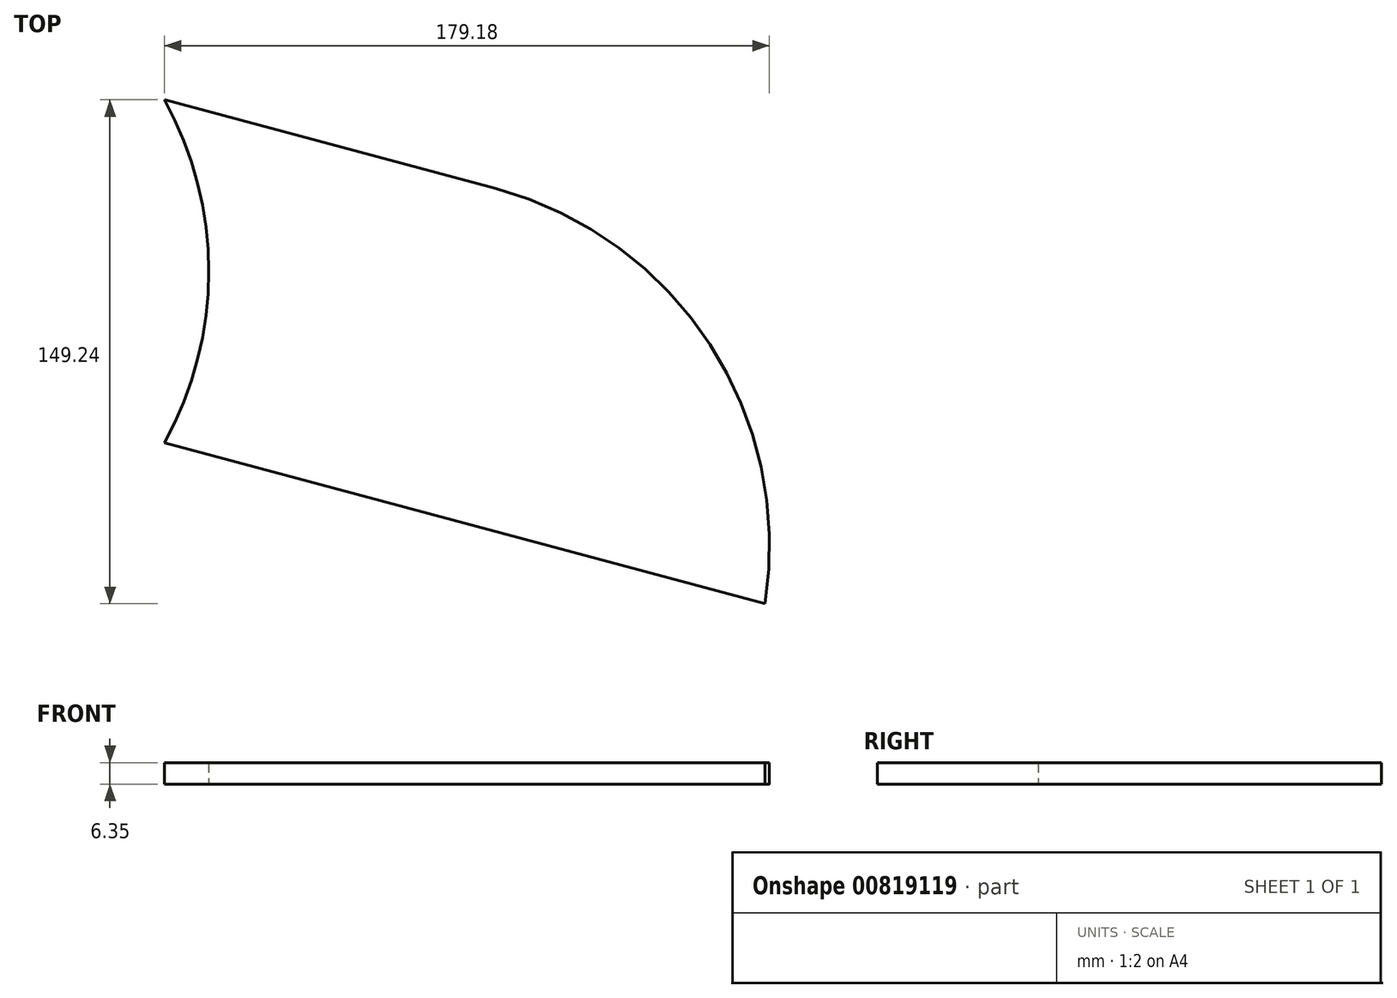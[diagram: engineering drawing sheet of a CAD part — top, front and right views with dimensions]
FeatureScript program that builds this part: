
annotation { "Feature Type Name" : "Feature", "Feature Type Description" : "" }
export const myFeature = defineFeature(function(context is Context, id is Id, definition is map)
    precondition{}
    {
        {
            var Q0;
            Q0=qCreatedBy(makeId("Top.planeOp"),FACE);
            var sketch = newSketch(context, id + "F0", { "sketchPlane" : qUnion([Q0])});
            skLineSegment(sketch, "E0", {"start": v(0, 0) * mm, "end": v(177.8, -47.64) * mm});
            skArc(sketch, "E1", {"start": v(177.8, -47.64) * mm, "mid": v(161.6, 29.14) * mm, "end": v(98.14, 75.3) * mm});
            skArc(sketch, "E2", {"start": v(0, 0) * mm, "mid": v(13.17, 50.8) * mm, "end": v(0, 101.6) * mm});
            skLineSegment(sketch, "E3", {"start": v(98.14, 75.3) * mm, "end": v(0, 101.6) * mm});
            skSolve(sketch);
        }
        {
            var Q0;
            Q0 = qSketchRegion(id + "F0", true);
            extrude(context, id + "F1", {"entities" : qUnion([Q0]), "depth" : 6.35 * mm, "offsetDistance" : 25.4 * mm});
        }
    });
